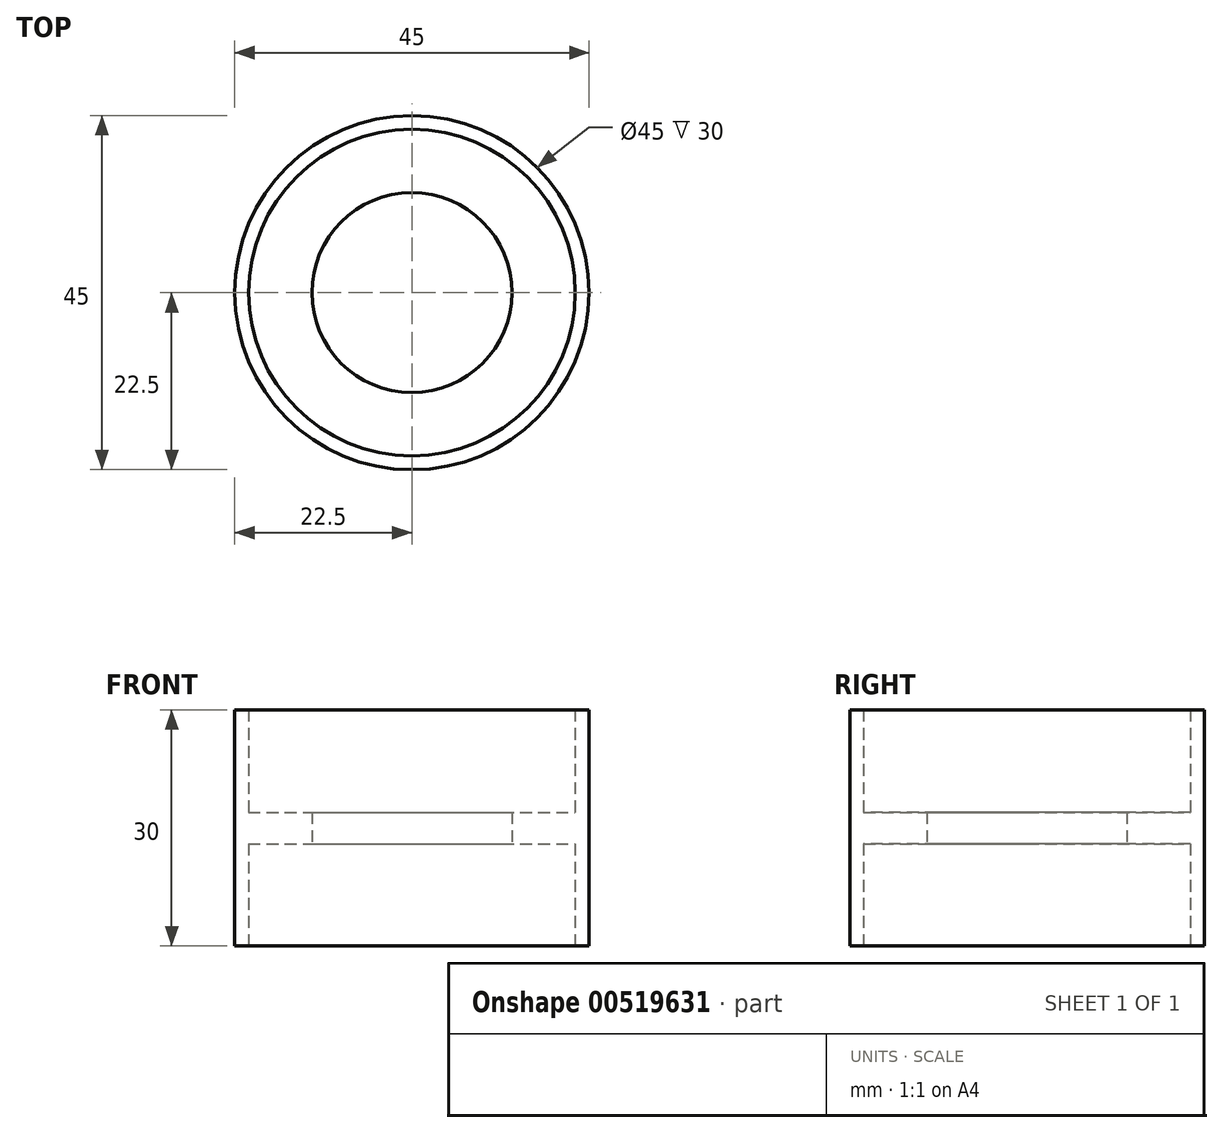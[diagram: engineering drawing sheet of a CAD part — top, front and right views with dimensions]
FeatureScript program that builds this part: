
annotation { "Feature Type Name" : "Feature", "Feature Type Description" : "" }
export const myFeature = defineFeature(function(context is Context, id is Id, definition is map)
    precondition{}
    {
        {
            var Q0;
            Q0=qCreatedBy(makeId("Front.planeOp"),FACE);
            var sketch = newSketch(context, id + "F0", { "sketchPlane" : qUnion([Q0])});
            skLineSegment(sketch, "E0", {"start": v(22.5, 15.07) * mm, "end": v(22.5, -14.93) * mm});
            skLineSegment(sketch, "E1", {"start": v(20.75, -14.93) * mm, "end": v(22.5, -14.93) * mm});
            skLineSegment(sketch, "E2", {"start": v(20.75, -14.93) * mm, "end": v(20.75, -1.93) * mm});
            skLineSegment(sketch, "E3", {"start": v(20.75, -1.93) * mm, "end": v(12.7, -1.93) * mm});
            skLineSegment(sketch, "E4", {"start": v(12.7, -1.93) * mm, "end": v(12.7, 2.07) * mm});
            skLineSegment(sketch, "E5", {"start": v(12.7, 2.07) * mm, "end": v(20.75, 2.07) * mm});
            skLineSegment(sketch, "E6", {"start": v(20.75, 2.07) * mm, "end": v(20.75, 15.07) * mm});
            skLineSegment(sketch, "E7", {"start": v(20.75, 15.07) * mm, "end": v(22.5, 15.07) * mm});
            skLineSegment(sketch, "E8", {"start": v(0, 31.93) * mm, "end": v(0, -32.29) * mm, "construction": true});
            skSolve(sketch);
        }
        {
            var Q0;
            Q0 = qConstructionFilter(qBodyType(qCreatedBy(id + "F0" ,EDGE), BodyType.WIRE), ConstructionObject.NO);
            var Q1;
            Q1=sQuery(id+"F0.wireOp",EDGE,"E8");
            revolve(context, id + "F1", {"bodyType" : ToolBodyType.SURFACE, "surfaceEntities" : qUnion([Q0]), "axis" : qUnion([Q1]), "revolveType" : RevolveType.FULL});
        }
    });
